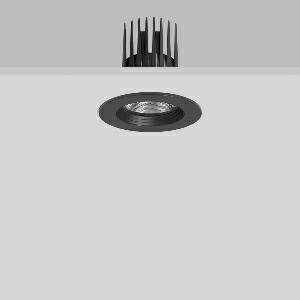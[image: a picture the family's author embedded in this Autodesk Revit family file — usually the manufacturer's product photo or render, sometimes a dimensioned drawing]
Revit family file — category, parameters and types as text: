
# Revit family: heledon_mini_e_901748_003_1_76_5158
name_source: partatom
category: Lighting Fixtures
units: mm (PartAtom-declared; Revit-internal decimal feet)

## family parameters
Cut with Voids When Loaded = No
Host = Face
Light Source = No
Part Type = Normal
Room Calculation Point = No
Round Connector Dimension = Use Diameter
Shared = No

## types (1)
- HELEDON mini E (1 x LED Modul 940, 3800 lm, 4000)
    Apparent Load = 29 VA
    Approval mark = CE
    CIE Flux Codes = 100 100 100 100 100
    Color Rendering = 92
    Color Temperature = 4000
    Default Elevation = 1800 mm
    Description = Series: HELEDON mini
Round recessed downlight. Housing: die-cast aluminium, powder-coated. Black plastic ring and recessed LED to prevent glare from the side. Optical assembly with reflector made of MIRO-Silver with 98% total light reflection for outstanding efficiency - can be changed without tools. Best colour rendering index Ra>90. Suitable for Recessed ceiling mounting. Installation without tools thanks to spring fastening system. Including separate LED converter with connecting cable 600 mm.High quality converter without flickering and stroboscopic effect. Through-wiring box (5 pole) available as accessory. The following accessories can be mounted without use of tools: interchangeable lenses, decorative glasses, honeycomb louvre, clear and frosted diffusers, white interchangeable plastic ring. 
Colour: deep black, matt (RAL 9005)
Diameter: 124 mm
Height: 3 mm
Cut-out diameter: 114 mm
Recess height: 170 mm
Luminaire: recess height: 120 mm
Lamp: LED
Socket: without socket
Colour temperature: 4000K
Colour rendering index (CRI): 92
System power: 29 W
Rated luminous flux: 3800 lm
Luminous efficiency: 131 lm/W
Control gear: Converter, dimmable, DALI
Protection class: II
Type of protection: IP 20
    Height = 0 mm  [stored 0 ft]
    Lamp = 1 x LED Modul 940
    Lamp Light Flux = 3800 lm
    Lamp count = 1
    Length = 124 mm  [stored 0.406824 ft]
    Lifetime = 50000 h
    Luminous efficacy = 131 lm/W
    Manufacturer = RZB
    ModVariant = No
    Model = 901748.003.1.76
    Mounting Place = Ceiling
    Mounting Type = Recessed
    Number of Poles = 1
    OnlyDefault = Yes
    Power Factor = 1
    Product Name = HELEDON mini E
    Product group = Recessed downlights
    ProductGroupID = 402
    Protection Class = Protection class II
    Protection Degree = IP 20
    RLX_Detail_Level = 1
    RLX_Emergency_Light_Flux = 0 lm
    RLX_Emergency_Type = 0
    RLX_Emergency_Type_DB = No
    RlxData = <blob elided: 127865 chars, md5=18036da2>
    Socket = socket
    Standby Power = 0 W
    System Light Flux = 3800 lm
    System Power = 29 W
    Type Comments = Product without accessories
    Type Image = 901657.003.jpg
    URL = http://relux.com
    VarID = ---
    Voltage = 230 V
    Voltage Range = 220-240 V
    Weight = 0.00 kg
    Width = 0 mm  [stored 0 ft]

note: [stored X ft] marks values corroborated as IEEE doubles in the binary element streams (Revit-internal decimal feet)

## geometry (parser evidence)
native form markers: Blend x4, Sweep x12
no freeform markers — native parametric forms only
